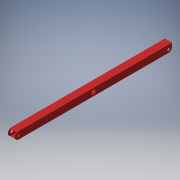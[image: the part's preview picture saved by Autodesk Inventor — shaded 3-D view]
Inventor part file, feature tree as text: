
AUTODESK INVENTOR PART (.ipt)
format: ipt  version: 2017 SP1 (Build 210196100, 196)  size: 148,480 bytes
history: native  units: in
note: dims shown in document units (in); Inventor stores cm internally (conversion verified against a paired STEP export)
features: extrude x3, sketch x3, projected_geometry x1
ambient origin geometry x8: Origin, YZ Plane, XZ Plane, XY Plane, X Axis, Y Axis, Z Axis, Center Point
bodies: Solid1 (feature_tree)
feature tree (7):
  extrude  "Extrusion1"  Depth=1.0in
  extrude  "Extrusion2"  Depth=0.0625in TaperAngle=0.0deg
  extrude  "Extrusion4"  Depth=1.0in
  sketch  "Sketch1"  dims[d0=1.0in d1=1.0in]
  sketch  "Sketch2"  dims[d2=0.0625in d3=22.0in d4=0.0in]
  sketch  "Sketch4"  dims[d5=0.625in d6=0.375in d8=1.0in d9=0.0in d13=0.5in d14=0.3866in d15=1.0in d16=0.5in d17=1.0in d18=0.0in]
  projected_geometry  "Projected Loop1"
